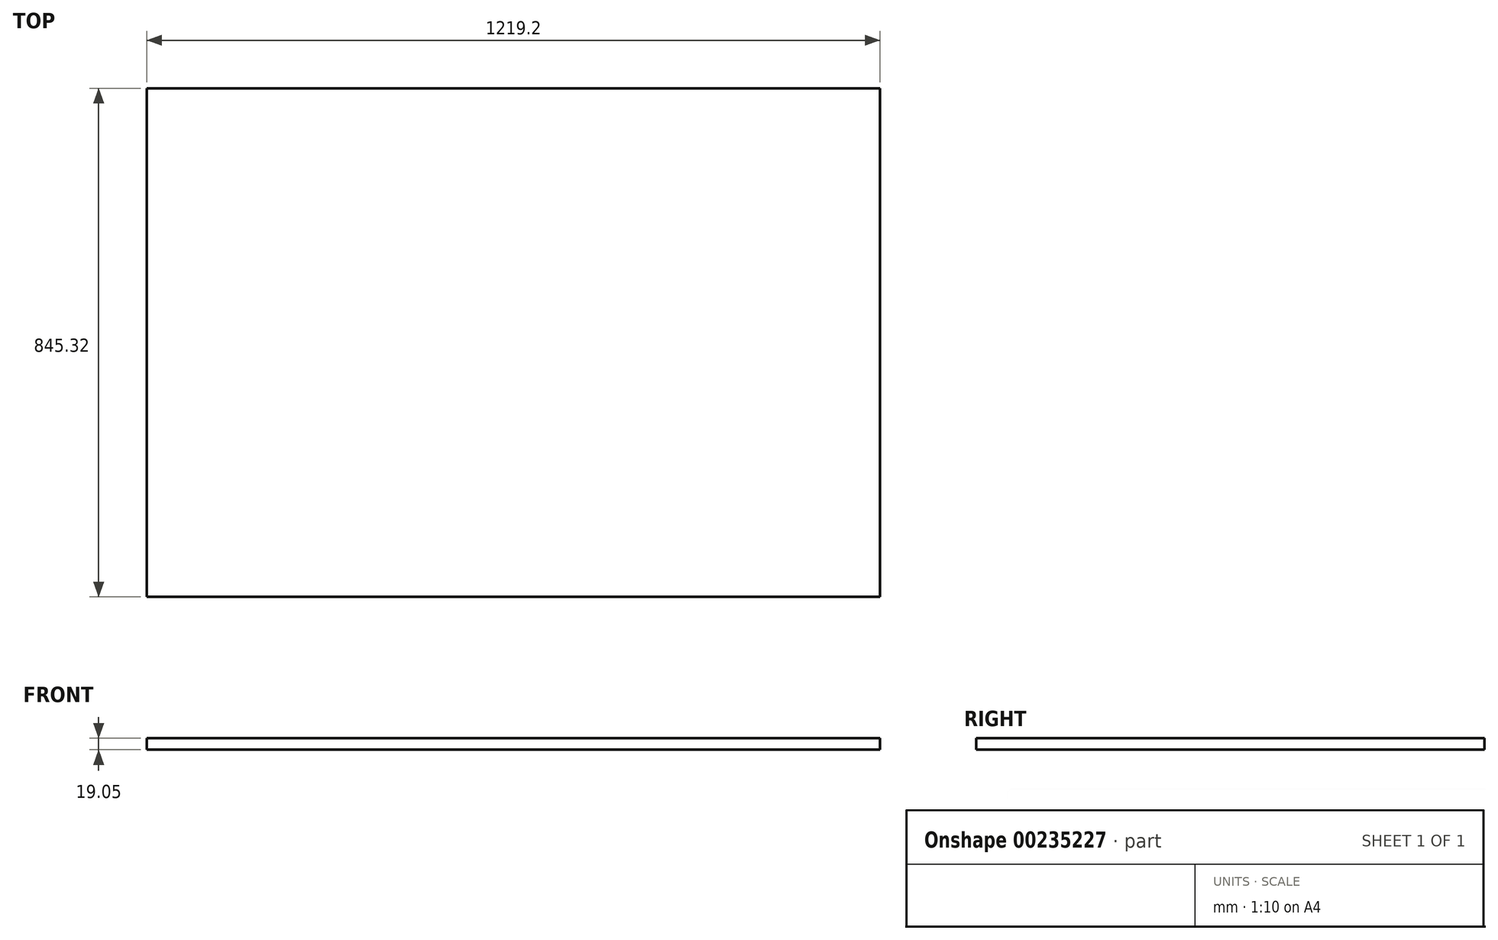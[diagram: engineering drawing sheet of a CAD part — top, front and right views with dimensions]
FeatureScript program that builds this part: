
annotation { "Feature Type Name" : "Feature", "Feature Type Description" : "" }
export const myFeature = defineFeature(function(context is Context, id is Id, definition is map)
    precondition{}
    {
        {
            var Q0;
            Q0=qCreatedBy(makeId("Top.planeOp"),FACE);
            var sketch = newSketch(context, id + "F0", { "sketchPlane" : qUnion([Q0])});
            skLineSegment(sketch, "E0.bottom", {"start": v(-609.6, 422.66) * mm, "end": v(609.6, 422.66) * mm});
            skLineSegment(sketch, "E0.top", {"start": v(-609.6, -422.66) * mm, "end": v(609.6, -422.66) * mm});
            skLineSegment(sketch, "E0.left", {"start": v(-609.6, 422.66) * mm, "end": v(-609.6, -422.66) * mm});
            skLineSegment(sketch, "E0.right", {"start": v(609.6, 422.66) * mm, "end": v(609.6, -422.66) * mm});
            skLineSegment(sketch, "E1", {"start": v(0, 422.66) * mm, "end": v(0, -422.66) * mm, "construction": true});
            skLineSegment(sketch, "E2", {"start": v(-609.6, 0) * mm, "end": v(609.6, 0) * mm, "construction": true});
            skSolve(sketch);
        }
        {
            var Q0;
            Q0=makeQuery(id+"F0.imprint","IMPRINT",FACE,{"disambiguationData":[TD([[makeQuery(id+"F0.imprint","IMPRINT",EDGE,{"derivedFrom":sQuery(id+"F0.wireOp",EDGE,"E0.bottom")}),-1.0]])]});
            extrude(context, id + "F1", {"entities" : qUnion([Q0]), "depth" : 19.05 * mm});
        }
    });
